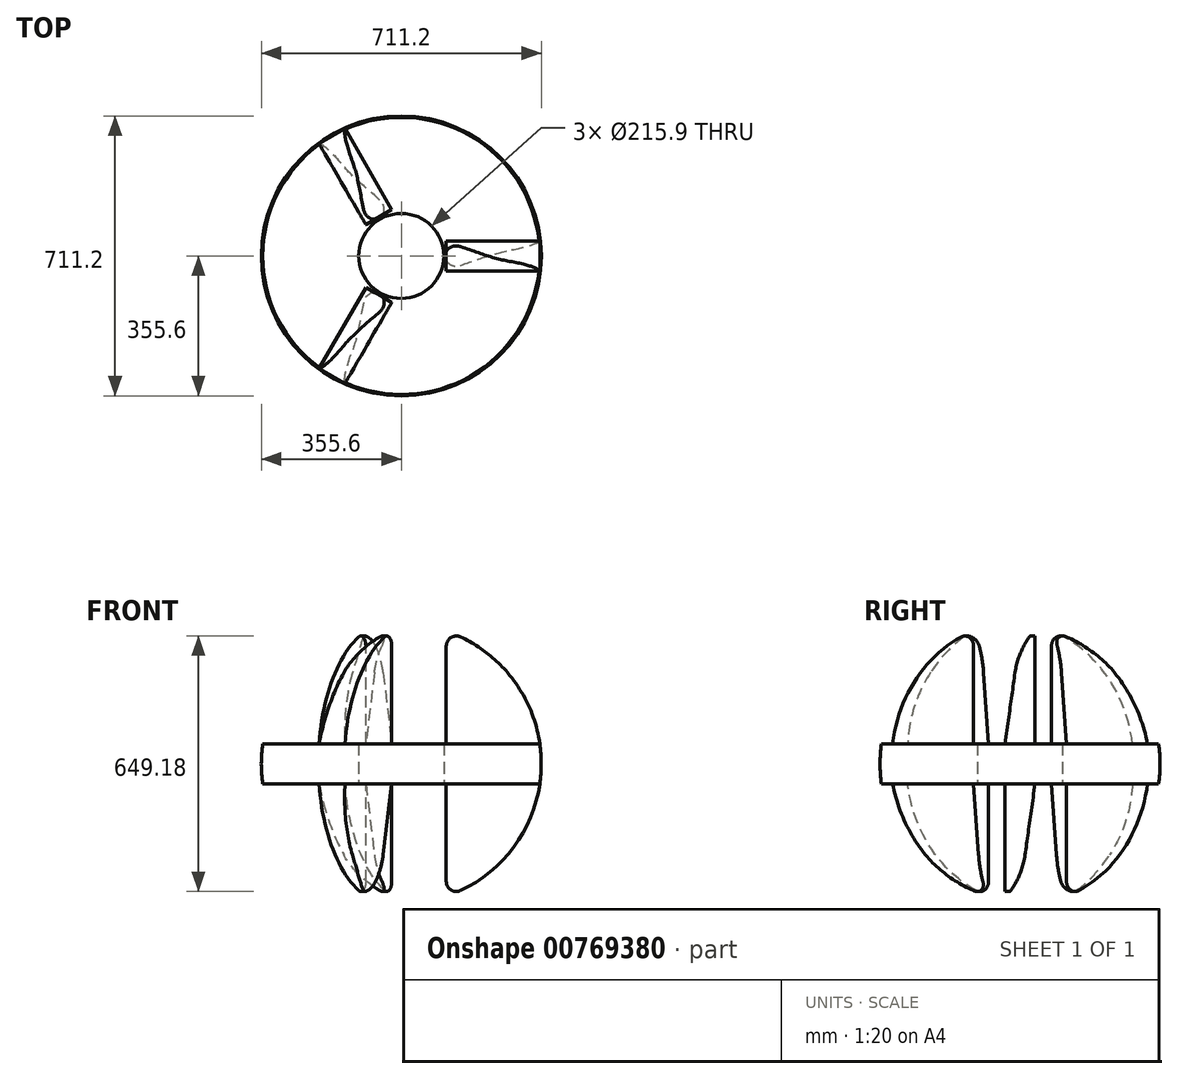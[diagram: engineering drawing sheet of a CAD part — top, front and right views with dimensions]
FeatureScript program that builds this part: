
annotation { "Feature Type Name" : "Feature", "Feature Type Description" : "" }
export const myFeature = defineFeature(function(context is Context, id is Id, definition is map)
    precondition{}
    {
        {
            var Q0;
            Q0=qCreatedBy(makeId("Front.planeOp"),FACE);
            var sketch = newSketch(context, id + "F0", { "sketchPlane" : qUnion([Q0])});
            skLineSegment(sketch, "E0", {"start": v(0, 0) * mm, "end": v(0, 719.83) * mm, "construction": true});
            skLineSegment(sketch, "E1", {"start": v(381, 750.81) * mm, "end": v(381, -112.59) * mm, "construction": true});
            skLineSegment(sketch, "E2", {"start": v(-124.84, 649.18) * mm, "end": v(765.44, 649.18) * mm, "construction": true});
            skLineSegment(sketch, "E3", {"start": v(114.3, 25.4) * mm, "end": v(114.3, 273.8) * mm});
            skLineSegment(sketch, "E4", {"start": v(107.95, 375.4) * mm, "end": v(107.95, 273.8) * mm});
            skLineSegment(sketch, "E5", {"start": v(0, 324.6) * mm, "end": v(640.71, 324.6) * mm, "construction": true});
            skLineSegment(sketch, "E6", {"start": v(351.95, 273.8) * mm, "end": v(114.3, 273.8) * mm});
            skLineSegment(sketch, "E7", {"start": v(114.3, 375.4) * mm, "end": v(351.95, 375.4) * mm});
            skArc(sketch, "E8", {"start": v(351.95, 273.8) * mm, "mid": v(355.6, 324.6) * mm, "end": v(351.95, 375.4) * mm});
            skArc(sketch, "E9.trimOffspring", {"start": v(150.45, 2.39) * mm, "mid": v(285.51, 112.61) * mm, "end": v(351.95, 273.8) * mm});
            skLineSegment(sketch, "E10.trimOffspring", {"start": v(114.3, 375.4) * mm, "end": v(114.3, 623.78) * mm});
            skLineSegment(sketch, "E11", {"start": v(107.95, 273.8) * mm, "end": v(114.3, 273.8) * mm});
            skLineSegment(sketch, "E12", {"start": v(107.95, 375.4) * mm, "end": v(114.3, 375.4) * mm});
            skArc(sketch, "E13.filletArc", {"start": v(114.3, 25.4) * mm, "mid": v(126.06, 3.97) * mm, "end": v(150.45, 2.39) * mm});
            skArc(sketch, "E14.filletArc", {"start": v(150.45, 646.8) * mm, "mid": v(126.06, 645.2) * mm, "end": v(114.3, 623.78) * mm});
            skArc(sketch, "E15", {"start": v(351.95, 375.4) * mm, "mid": v(285.51, 536.57) * mm, "end": v(150.45, 646.8) * mm});
            skSolve(sketch);
        }
        {
            var Q0;
            Q0=makeQuery(id+"F0.imprint","IMPRINT",FACE,{"disambiguationData":[TD([[makeQuery(id+"F0.imprint","IMPRINT",EDGE,{"derivedFrom":sQuery(id+"F0.wireOp",EDGE,"E4")}),1.0]])]});
            var Q1;
            Q1=sQuery(id+"F0.wireOp",EDGE,"E0");
            revolve(context, id + "F1", {"surfaceOperationType" : NewSurfaceOperationType.NEW, "entities" : qUnion([Q0]), "axis" : qUnion([Q1]), "revolveType" : RevolveType.FULL});
        }
        {
            var Q0;
            Q0=makeQuery(id+"F0.imprint","IMPRINT",FACE,{"disambiguationData":[TD([[makeQuery(id+"F0.imprint","IMPRINT",EDGE,{"derivedFrom":sQuery(id+"F0.wireOp",EDGE,"E7")}),1.0]])]});
            var Q1;
            Q1=makeQuery(id+"F0.imprint","IMPRINT",FACE,{"disambiguationData":[TD([[makeQuery(id+"F0.imprint","IMPRINT",EDGE,{"derivedFrom":sQuery(id+"F0.wireOp",EDGE,"E3")}),-1.0]])]});
            extrude(context, id + "F2", {"entities" : qUnion([Q0, Q1]), "operationType" : NewBodyOperationType.ADD, "endBound" : BoundingType.SYMMETRIC, "depth" : 76.2 * mm, "offsetDistance" : 25.4 * mm});
        }
        {
            var Q0;
            Q0=qCreatedBy(makeId("Right.planeOp"),FACE);
            var sketch = newSketch(context, id + "F3", { "sketchPlane" : qUnion([Q0])});
            skLineSegment(sketch, "E16", {"start": v(-12.7, 556.07) * mm, "end": v(-38.1, 375.4) * mm});
            skCircle(sketch, "E17", {"center": v(0, 324.6) * mm, "radius": 355.6 * mm, "construction": true});
            skLineSegment(sketch, "E18", {"start": v(0, 324.6) * mm, "end": v(-249.76, 757.18) * mm, "construction": true});
            skLineSegment(sketch, "E19", {"start": v(-114.3, 705.13) * mm, "end": v(-114.3, 114.82) * mm, "construction": true});
            skLineSegment(sketch, "E20", {"start": v(-38.1, 375.4) * mm, "end": v(-89.45, 375.4) * mm});
            skLineSegment(sketch, "E21", {"start": v(-89.45, 375.4) * mm, "end": v(-89.45, 729.88) * mm});
            skLineSegment(sketch, "E22", {"start": v(121.26, 273.8) * mm, "end": v(38.1, 273.8) * mm});
            skLineSegment(sketch, "E23", {"start": v(38.1, 273.8) * mm, "end": v(12.7, 93.11) * mm});
            skLineSegment(sketch, "E24", {"start": v(121.26, -81.8) * mm, "end": v(121.26, 273.8) * mm});
            skArc(sketch, "E25", {"start": v(-12.7, 556.07) * mm, "mid": v(47.38, 673.98) * mm, "end": v(167.32, 729.88) * mm});
            skLineSegment(sketch, "E26", {"start": v(167.32, 729.88) * mm, "end": v(-89.45, 729.88) * mm});
            skArc(sketch, "E27", {"start": v(12.7, 93.11) * mm, "mid": v(-55.2, -31.96) * mm, "end": v(-188.52, -81.8) * mm});
            skLineSegment(sketch, "E28", {"start": v(-188.52, -81.8) * mm, "end": v(121.26, -81.8) * mm});
            skSolve(sketch);
        }
        {
            var Q0;
            Q0=makeQuery(id+"F3.imprint","IMPRINT",FACE,{"disambiguationData":[TD([[makeQuery(id+"F3.imprint","IMPRINT",EDGE,{"derivedFrom":sQuery(id+"F3.wireOp",EDGE,"E16")}),-1.0]])]});
            var Q1;
            Q1=makeQuery(id+"F3.imprint","IMPRINT",FACE,{"disambiguationData":[TD([[makeQuery(id+"F3.imprint","IMPRINT",EDGE,{"derivedFrom":sQuery(id+"F3.wireOp",EDGE,"E22")}),1.0]])]});
            extrude(context, id + "F4", {"entities" : qUnion([Q0, Q1]), "operationType" : NewBodyOperationType.REMOVE, "endBound" : BoundingType.THROUGH_ALL, "depth" : 25.4 * mm, "offsetDistance" : 25.4 * mm});
        }
        {
            var Q0;
            Q0=makeQuery(id+"F1.opRevolve","SWEPT_BODY",BODY,{"disambiguationData":[OSD([sQuery(id+"F0.wireOp",EDGE,"E4"),sQuery(id+"F0.wireOp",EDGE,"E6"),sQuery(id+"F0.wireOp",EDGE,"E7"),sQuery(id+"F0.wireOp",EDGE,"E8"),sQuery(id+"F0.wireOp",EDGE,"E11"),sQuery(id+"F0.wireOp",EDGE,"E12")])]});
            var Q1;
            Q1=sQuery(id+"F0.wireOp",EDGE,"E0");
            circularPattern(context, id + "F5", {"entities" : qUnion([Q0]), "axis" : qUnion([Q1]), "angle" : 360 * degree, "instanceCount" : 3, "equalSpace" : true});
        }
    });
